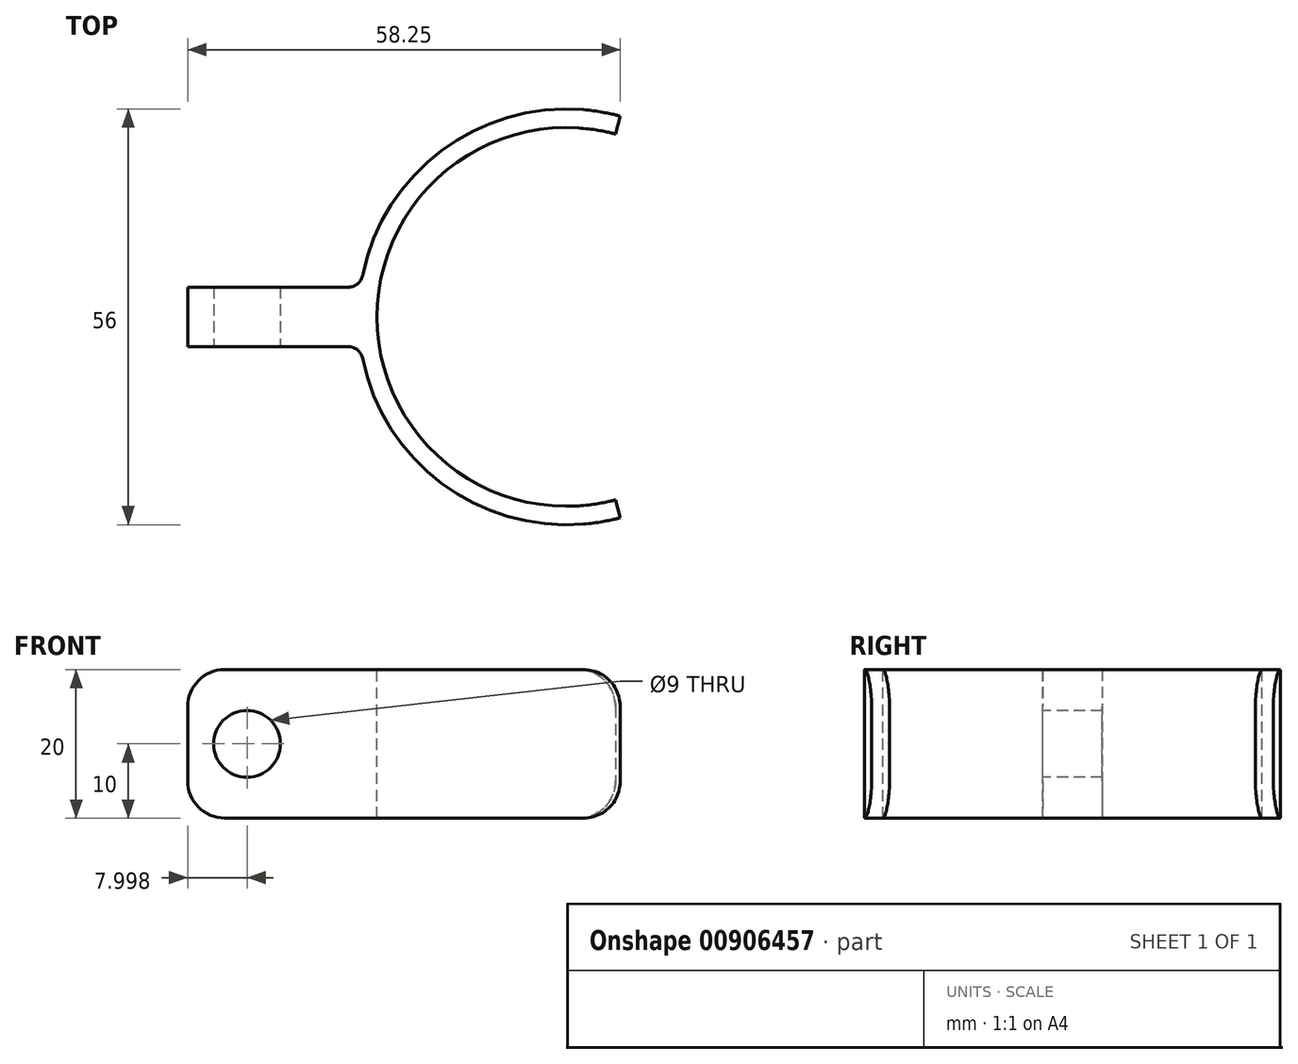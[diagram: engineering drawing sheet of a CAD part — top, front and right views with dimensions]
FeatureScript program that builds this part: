
annotation { "Feature Type Name" : "Feature", "Feature Type Description" : "" }
export const myFeature = defineFeature(function(context is Context, id is Id, definition is map)
    precondition{}
    {
        {
            var Q0;
            Q0=qCreatedBy(makeId("Front.planeOp"),FACE);
            var sketch = newSketch(context, id + "F0", { "sketchPlane" : qUnion([Q0])});
            skLineSegment(sketch, "E0", {"start": v(17.35, 10) * mm, "end": v(17.35, -10) * mm});
            skLineSegment(sketch, "E1", {"start": v(17.35, -10) * mm, "end": v(14.85, -10) * mm});
            skLineSegment(sketch, "E2", {"start": v(14.85, -10) * mm, "end": v(14.85, 10) * mm});
            skLineSegment(sketch, "E3", {"start": v(14.85, 10) * mm, "end": v(17.35, 10) * mm});
            skLineSegment(sketch, "E4", {"start": v(42.85, 10) * mm, "end": v(42.85, -16.64) * mm});
            skLineSegment(sketch, "E5", {"start": v(14.85, 10) * mm, "end": v(-0.15, 10) * mm});
            skLineSegment(sketch, "E6", {"start": v(14.85, -10) * mm, "end": v(-0.15, -10) * mm});
            skLineSegment(sketch, "E7", {"start": v(-8.15, -1.75) * mm, "end": v(-8.15, -10) * mm});
            skLineSegment(sketch, "E8", {"start": v(-0.15, -10) * mm, "end": v(-8.15, -10) * mm});
            skLineSegment(sketch, "E9", {"start": v(-8.15, -1.75) * mm, "end": v(-8.15, 10) * mm});
            skLineSegment(sketch, "E10", {"start": v(-8.15, 10) * mm, "end": v(-0.15, 10) * mm});
            skSolve(sketch);
        }
        {
            var Q0;
            Q0=makeQuery(id+"F0.imprint","IMPRINT",FACE,{"disambiguationData":[TD([[makeQuery(id+"F0.imprint","IMPRINT",EDGE,{"derivedFrom":sQuery(id+"F0.wireOp",EDGE,"E0")}),-1.0]])]});
            var Q1;
            Q1=sQuery(id+"F0.wireOp",EDGE,"E4");
            revolve(context, id + "F1", {"surfaceOperationType" : NewSurfaceOperationType.NEW, "entities" : qUnion([Q0]), "axis" : qUnion([Q1]), "revolveType" : RevolveType.SYMMETRIC, "angle" : 210 * degree});
        }
        {
            var Q0;
            Q0=makeQuery(id+"F0.imprint","IMPRINT",FACE,{"disambiguationData":[TD([[makeQuery(id+"F0.imprint","IMPRINT",EDGE,{"derivedFrom":sQuery(id+"F0.wireOp",EDGE,"E2")}),1.0]])]});
            var Q1;
            Q1=makeQuery(id+"F0.imprint","IMPRINT",FACE,{"disambiguationData":[TD([[makeQuery(id+"F0.imprint","IMPRINT",EDGE,{"derivedFrom":sQuery(id+"F0.wireOp",EDGE,"E0")}),-1.0]])]});
            extrude(context, id + "F2", {"entities" : qUnion([Q0, Q1]), "operationType" : NewBodyOperationType.ADD, "endBound" : BoundingType.SYMMETRIC, "depth" : 8 * mm, "offsetDistance" : 25 * mm});
        }
        {
            var Q0;
            Q0=makeQuery(id+"F2.opExtrude","CAP_FACE",FACE,{"disambiguationData":[OSD([sQuery(id+"F0.wireOp",EDGE,"E0"),sQuery(id+"F0.wireOp",EDGE,"E1"),sQuery(id+"F0.wireOp",EDGE,"E3"),sQuery(id+"F0.wireOp",EDGE,"E5"),sQuery(id+"F0.wireOp",EDGE,"yzQiNmdZ-E5Vl-Feje-jFLp-P0w3TQD3PNfw"),sQuery(id+"F0.wireOp",EDGE,"E6")])],"isStart":false});
            var sketch = newSketch(context, id + "F3", { "sketchPlane" : qUnion([Q0])});
            skLineSegment(sketch, "E11", {"start": v(-0.15, 10) * mm, "end": v(-0.15, 0) * mm});
            skSolve(sketch);
        }
        {
            var Q0;
            Q0=sQuery(id+"F3.wireOp",VERTEX,"1e4gFdpg-3487-qhrq-Ahoh-itLQtgonZcL9.end");
            var Q1;
            Q1=sQuery(id+"F3.wireOp",VERTEX,"E11.end");
            var Q2;
            Q2=makeQuery(id+"F1.opRevolve","SWEPT_BODY",BODY,{"disambiguationData":[OSD([sQuery(id+"F0.wireOp",EDGE,"E0"),sQuery(id+"F0.wireOp",EDGE,"E1"),sQuery(id+"F0.wireOp",EDGE,"E2"),sQuery(id+"F0.wireOp",EDGE,"E3")])]});
            hole(context, id + "F4", {"style" : HoleStyle.SIMPLE, "endStyle" : HoleEndStyle.THROUGH, "standardTappedOrClearance" : lookupTablePath({ "fit" : "Normal", "standard" : "ISO", "size" : "M8", "type" : "Clearance" }), "standardBlindInLast" : lookupTablePath({ "fit" : "Normal", "standard" : "ISO", "size" : "M8", "type" : "Clearance" }), "holeDiameter" : 9 * mm, "majorDiameter" : 5 * mm, "isTappedThrough" : true, "tappedDepth" : 12 * mm, "tapClearance" : 3, "locations" : qUnion([Q0, Q1]), "scope" : qUnion([Q2])});
        }
        {
            var Q0;
            Q0=makeQuery(id+"F2.boolean.opBoolean","INTERSECT",EDGE,{"derivedFrom":[makeQuery(id+"F1.opRevolve","SWEPT_FACE",FACE,{"disambiguationData":[OSD([sQuery(id+"F0.wireOp",EDGE,"E2")])]}),makeQuery(id+"F2.opExtrude","CAP_FACE",FACE,{"disambiguationData":[OSD([sQuery(id+"F0.wireOp",EDGE,"E0"),sQuery(id+"F0.wireOp",EDGE,"E1"),sQuery(id+"F0.wireOp",EDGE,"E3"),sQuery(id+"F0.wireOp",EDGE,"E5"),sQuery(id+"F0.wireOp",EDGE,"E6"),sQuery(id+"F0.wireOp",EDGE,"21a918c3-e08d-4af3-b726-0d48416c87b2.filletArc"),sQuery(id+"F0.wireOp",EDGE,"45fa9057-b76a-488c-a190-e3a83fbb6511.filletArc")])],"isStart":false})]});
            var Q1;
            Q1=makeQuery(id+"F2.boolean.opBoolean","INTERSECT",EDGE,{"derivedFrom":[makeQuery(id+"F1.opRevolve","SWEPT_FACE",FACE,{"disambiguationData":[OSD([sQuery(id+"F0.wireOp",EDGE,"E2")])]}),makeQuery(id+"F2.opExtrude","CAP_FACE",FACE,{"disambiguationData":[OSD([sQuery(id+"F0.wireOp",EDGE,"E0"),sQuery(id+"F0.wireOp",EDGE,"E1"),sQuery(id+"F0.wireOp",EDGE,"E3"),sQuery(id+"F0.wireOp",EDGE,"E5"),sQuery(id+"F0.wireOp",EDGE,"E6"),sQuery(id+"F0.wireOp",EDGE,"21a918c3-e08d-4af3-b726-0d48416c87b2.filletArc"),sQuery(id+"F0.wireOp",EDGE,"45fa9057-b76a-488c-a190-e3a83fbb6511.filletArc")])],"isStart":true})]});
            fillet(context, id + "F5", {"entities" : qUnion([Q0, Q1]), "radius" : 2 * mm, "tangentPropagation" : true, "allowEdgeOverflow" : false});
        }
        {
            var Q0;
            Q0=makeQuery(id+"F1.opRevolve","CAP_EDGE",EDGE,{"disambiguationData":[OSD([sQuery(id+"F0.wireOp",EDGE,"E3")])],"isStart":true});
            var Q1;
            Q1=makeQuery(id+"F1.opRevolve","CAP_EDGE",EDGE,{"disambiguationData":[OSD([sQuery(id+"F0.wireOp",EDGE,"E1")])],"isStart":true});
            var Q2;
            Q2=makeQuery(id+"F1.opRevolve","CAP_EDGE",EDGE,{"disambiguationData":[OSD([sQuery(id+"F0.wireOp",EDGE,"E1")])],"isStart":false});
            var Q3;
            Q3=makeQuery(id+"F1.opRevolve","CAP_EDGE",EDGE,{"disambiguationData":[OSD([sQuery(id+"F0.wireOp",EDGE,"E3")])],"isStart":false});
            fillet(context, id + "F6", {"entities" : qUnion([Q0, Q1, Q2, Q3]), "radius" : 5 * mm, "tangentPropagation" : true, "allowEdgeOverflow" : false});
        }
        {
            var Q0;
            Q0=makeQuery(id+"F2.opExtrude","SWEPT_EDGE",EDGE,{"disambiguationData":[OSD([sQuery(id+"F0.wireOp",EDGE,"E9"),sQuery(id+"F0.wireOp",EDGE,"E10")])]});
            var Q1;
            Q1=makeQuery(id+"F2.opExtrude","SWEPT_EDGE",EDGE,{"disambiguationData":[OSD([sQuery(id+"F0.wireOp",EDGE,"E7"),sQuery(id+"F0.wireOp",EDGE,"E8")])]});
            fillet(context, id + "F7", {"entities" : qUnion([Q0, Q1]), "radius" : 5 * mm, "tangentPropagation" : true, "allowEdgeOverflow" : false});
        }
    });
